# Revit family: Sanitary_Taps-Mixers_hansgrohe_32539CHN-Metropol-Single-lever-basin-mix_1
name_source: partatom
category: Plumbing Fixtures
revit_build: Autodesk Revit 2018 (Build: 20170223_1515(x64)
units: mm (PartAtom-declared; Revit-internal decimal feet)

## family parameters
Always vertical = No
Cut with Voids When Loaded = No
OmniClass Number = 23.45.05.14
OmniClass Title = Plumbing Fixtures - Sanitary Washing Units
Part Type = Normal
Room Calculation Point = No
Round Connector Dimension = Use Diameter
Shared = No
Work Plane-Based = Yes

## types (1)
- 007 Chrome
    Always visible = Yes
    BIMobject category = Taps & Mixers
    Cold Water Inlet = 13 mm
    Default Elevation = 1219 mm
    Description = Metropol Single lever basin mixer 260 with lever handle for washbowls with waste set
    Design country = Germany
    EAN code = 4059625317082
    Edition number = 1
    GTIN code = https://4059625317082
    Hot Water Inlet = 13 mm
    IFC Classification = Valve
    Manufacturer = hansgrohe
    Manufacturer country = Germany
    Manufacturer name = hansgrohe
    Masterformat 2014 Code = 22 41 39
    Masterformat 2014 Description = Residential Faucets, Supplies, and Trim
    Material 1 = Hansgrohe - Metal - 007 Chrome
    Model = 32539CHN
    NBS Reference Code = 35-79-95
    NBS Reference Description = Wash Basin And Trough Water Supply Fittings
    OmniClass Code = 23-31 11 00
    OmniClass Description = Faucets
    Product Guid = 450f4e60-fc5e-4053-be5a-51325d8b8b7a
    Product SKU = 32539CHN
    Product data url = https://bimobject.com
    Product family = Metropol
    Product group = Basin mixers
    Product name = 32539CHN Metropol Single lever basin mixer 260 with lever handle for washbowls with waste set
    QR code = https://bimobject.com
    URL = https://www.hansgrohe.com
    Uniclass 2015 Code = Pr_40_20_87_98
    Uniclass 2015 Name = Washbasin taps
    Uniformat II Code = D2010
    Uniformat II Description = Plumbing Fixtures
    Weight Net (Kg) = 2.8

## geometry (parser evidence)
native form markers: Sweep x2
no freeform markers — native parametric forms only
